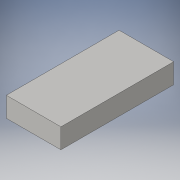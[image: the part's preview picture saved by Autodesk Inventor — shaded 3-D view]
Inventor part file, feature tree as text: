
AUTODESK INVENTOR PART (.ipt)
format: ipt  version: 2016 (Build 200138000, 138)  size: 84,480 bytes
history: native  units: in
note: dims shown in document units (in); Inventor stores cm internally (conversion verified against a paired STEP export)
features: extrude x1, sketch x1
ambient origin geometry x8: Origin, YZ Plane, XZ Plane, XY Plane, X Axis, Y Axis, Z Axis, Center Point
bodies: Solid1 (feature_tree)
feature tree (2):
  extrude  "Extrusion1"  Depth=2.7402in
  sketch  "Sketch1"  dims[d0=1.3268in d1=2.7402in d2=0.4843in d3=0.0in]
